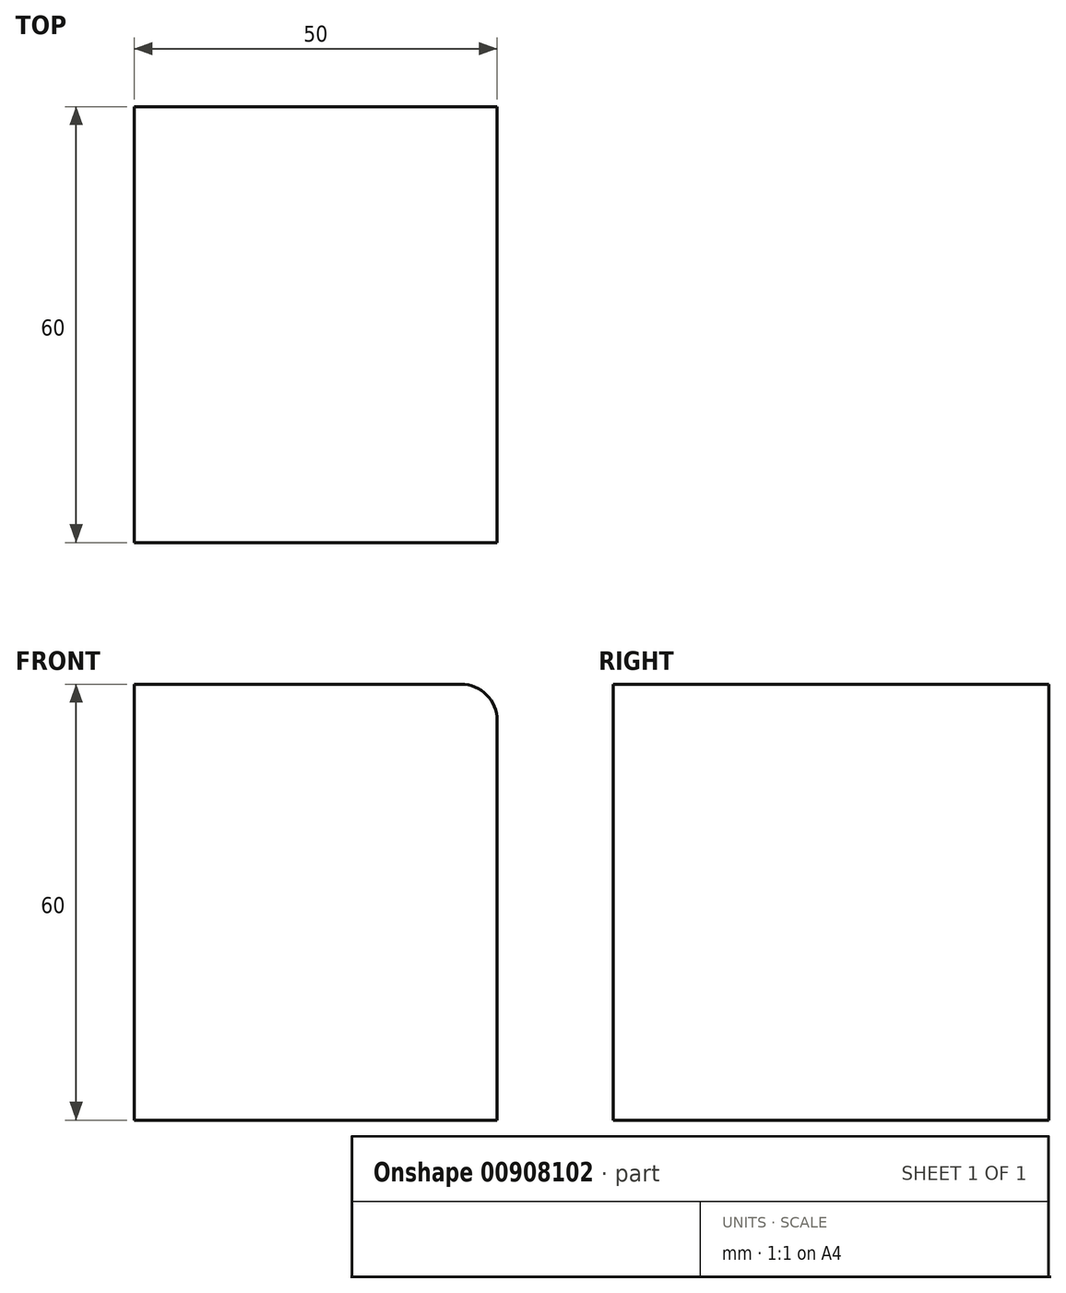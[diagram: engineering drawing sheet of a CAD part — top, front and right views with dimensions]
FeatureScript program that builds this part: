
annotation { "Feature Type Name" : "Feature", "Feature Type Description" : "" }
export const myFeature = defineFeature(function(context is Context, id is Id, definition is map)
    precondition{}
    {
        {
            var Q0;
            Q0=qCreatedBy(makeId("Top.planeOp"),FACE);
            var sketch = newSketch(context, id + "F0", { "sketchPlane" : qUnion([Q0])});
            skLineSegment(sketch, "E0.bottom", {"start": v(0, 0) * mm, "end": v(50, 0) * mm});
            skLineSegment(sketch, "E0.top", {"start": v(0, 60) * mm, "end": v(50, 60) * mm});
            skLineSegment(sketch, "E0.left", {"start": v(0, 0) * mm, "end": v(0, 60) * mm});
            skLineSegment(sketch, "E0.right", {"start": v(50, 0) * mm, "end": v(50, 60) * mm});
            skSolve(sketch);
        }
        {
            var Q0;
            Q0=makeQuery(id+"F0.imprint","IMPRINT",FACE,{"disambiguationData":[TD([[makeQuery(id+"F0.imprint","IMPRINT",EDGE,{"derivedFrom":sQuery(id+"F0.wireOp",EDGE,"E0.bottom")}),1.0]])]});
            extrude(context, id + "F1", {"entities" : qUnion([Q0]), "depth" : 60 * mm, "offsetDistance" : 25 * mm});
        }
        {
            var Q0;
            Q0=makeQuery(id+"F1.opExtrude","CAP_EDGE",EDGE,{"disambiguationData":[OSD([sQuery(id+"F0.wireOp",EDGE,"E0.right")])],"isStart":false});
            fillet(context, id + "F2", {"entities" : qUnion([Q0]), "tangentPropagation" : true, "radius" : 5 * mm, "defaultsChanged" : false, "vertexSettings" : [], "allowEdgeOverflow" : false});
        }
    });
